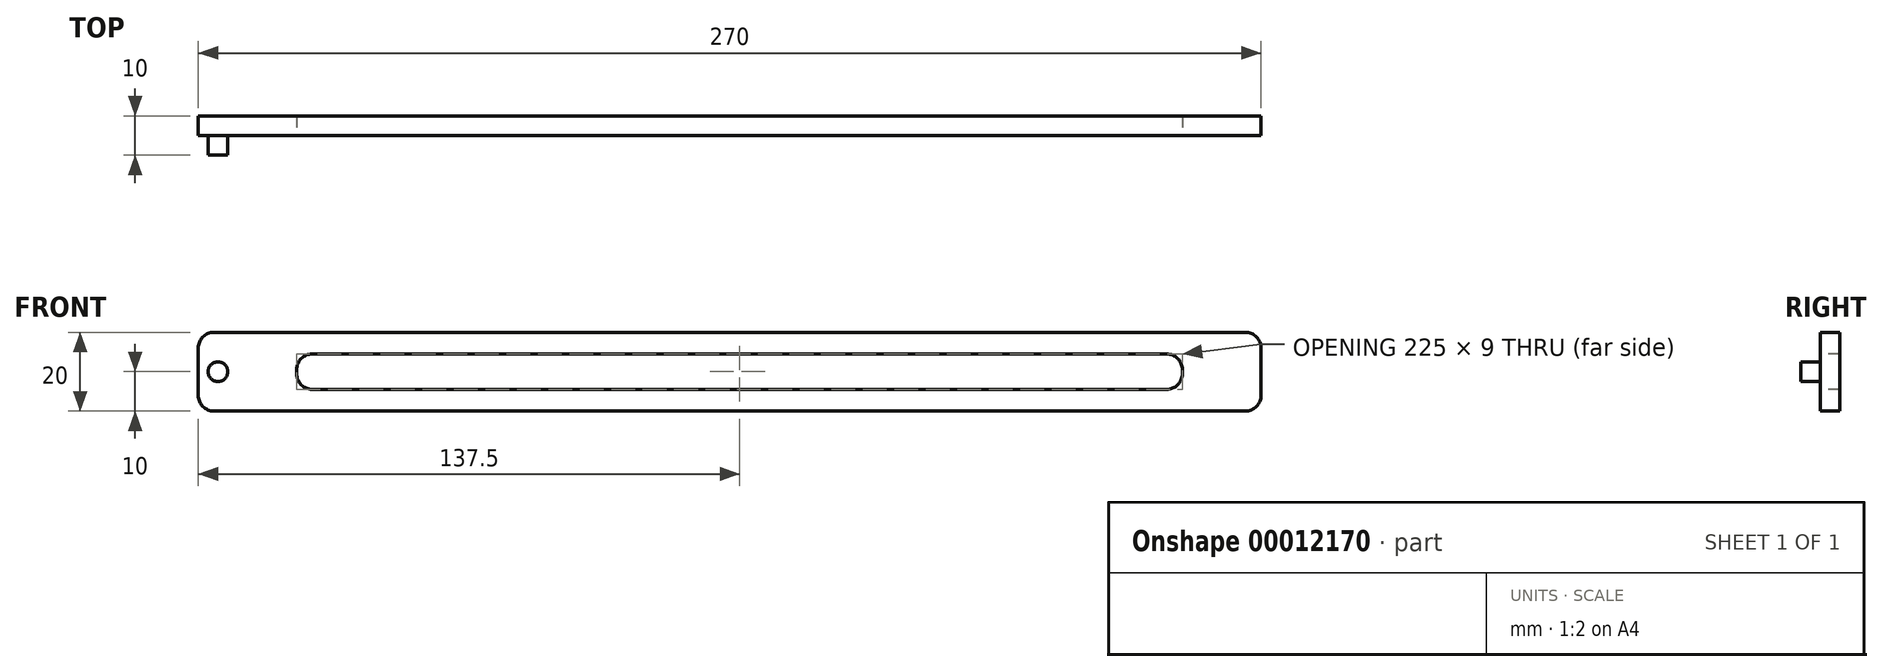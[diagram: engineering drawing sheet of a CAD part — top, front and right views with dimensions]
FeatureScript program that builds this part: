
annotation { "Feature Type Name" : "Feature", "Feature Type Description" : "" }
export const myFeature = defineFeature(function(context is Context, id is Id, definition is map)
    precondition{}
    {
        {
            var Q0;
            Q0=qCreatedBy(makeId("Right.planeOp"),FACE);
            var sketch = newSketch(context, id + "F0", { "sketchPlane" : qUnion([Q0])});
            skLineSegment(sketch, "E0.rect.bottom", {"start": v(2.5, -10) * mm, "end": v(-2.5, -10) * mm});
            skLineSegment(sketch, "E0.rect.top", {"start": v(2.5, 10) * mm, "end": v(-2.5, 10) * mm});
            skLineSegment(sketch, "E0.rect.left", {"start": v(2.5, -10) * mm, "end": v(2.5, 10) * mm});
            skLineSegment(sketch, "E0.rect.right", {"start": v(-2.5, -10) * mm, "end": v(-2.5, 10) * mm});
            skPoint(sketch, "E0.rect.middle", {"position": v(0, 0) * mm});
            skSolve(sketch);
        }
        {
            var Q0;
            Q0=makeQuery(id+"F0.imprint","IMPRINT",FACE,{"disambiguationData":[TD([[makeQuery(id+"F0.imprint","IMPRINT",EDGE,{"derivedFrom":sQuery(id+"F0.wireOp",EDGE,"E0.rect.bottom")}),-1.0]])]});
            extrude(context, id + "F1", {"entities" : qUnion([Q0]), "depth" : 110 * mm, "hasSecondDirection" : true, "secondDirectionOppositeDirection" : true, "secondDirectionDepth" : 160 * mm});
        }
        {
            var Q0;
            Q0=makeQuery(id+"F1.opExtrude","SWEPT_FACE",FACE,{"disambiguationData":[OSD([sQuery(id+"F0.wireOp",EDGE,"E0.rect.right")])]});
            var sketch = newSketch(context, id + "F2", { "sketchPlane" : qUnion([Q0])});
            skLineSegment(sketch, "E1", {"start": v(-160, 0) * mm, "end": v(-155, 0) * mm, "construction": true});
            skPoint(sketch, "E2.rect.middle", {"position": v(-155, 0) * mm});
            skCircle(sketch, "E3", {"center": v(-155, 0) * mm, "radius": 2.5 * mm});
            skSolve(sketch);
        }
        {
            var Q0;
            Q0=makeQuery(id+"F2.imprint","IMPRINT",FACE,{"disambiguationData":[TD([[makeQuery(id+"F2.imprint","IMPRINT",EDGE,{"derivedFrom":sQuery(id+"F2.wireOp",EDGE,"E3")}),1.0]])]});
            extrude(context, id + "F3", {"entities" : qUnion([Q0]), "operationType" : NewBodyOperationType.ADD, "depth" : 5 * mm});
        }
        {
            var Q0;
            Q0=makeQuery(id+"F1.opExtrude","SWEPT_FACE",FACE,{"disambiguationData":[OSD([sQuery(id+"F0.wireOp",EDGE,"E0.rect.right")])]});
            var sketch = newSketch(context, id + "F4", { "sketchPlane" : qUnion([Q0])});
            skLineSegment(sketch, "E4", {"start": v(110, 0) * mm, "end": v(90, 0) * mm, "construction": true});
            skLineSegment(sketch, "E5", {"start": v(90, 0) * mm, "end": v(90, 4.5) * mm, "construction": true});
            skLineSegment(sketch, "E6.bottom", {"start": v(90, 4.5) * mm, "end": v(-135, 4.5) * mm});
            skLineSegment(sketch, "E6.top", {"start": v(90, -4.5) * mm, "end": v(-135, -4.5) * mm});
            skLineSegment(sketch, "E6.left", {"start": v(90, 4.5) * mm, "end": v(90, -4.5) * mm});
            skLineSegment(sketch, "E6.right", {"start": v(-135, 4.5) * mm, "end": v(-135, -4.5) * mm});
            skSolve(sketch);
        }
        {
            var Q0;
            Q0=makeQuery(id+"F4.imprint","IMPRINT",FACE,{"disambiguationData":[TD([[makeQuery(id+"F4.imprint","IMPRINT",EDGE,{"derivedFrom":sQuery(id+"F4.wireOp",EDGE,"E6.bottom")}),1.0]])]});
            extrude(context, id + "F5", {"entities" : qUnion([Q0]), "operationType" : NewBodyOperationType.REMOVE, "endBound" : BoundingType.THROUGH_ALL, "oppositeDirection" : true, "depth" : 25 * mm});
        }
        {
            var Q0;
            Q0=makeQuery(id+"F1.opExtrude","CAP_EDGE",EDGE,{"disambiguationData":[OSD([sQuery(id+"F0.wireOp",EDGE,"E0.rect.top")])],"isStart":false});
            var Q1;
            Q1=makeQuery(id+"F1.opExtrude","CAP_EDGE",EDGE,{"disambiguationData":[OSD([sQuery(id+"F0.wireOp",EDGE,"E0.rect.bottom")])],"isStart":false});
            var Q2;
            Q2=makeQuery(id+"F1.opExtrude","CAP_EDGE",EDGE,{"disambiguationData":[OSD([sQuery(id+"F0.wireOp",EDGE,"E0.rect.top")])],"isStart":true});
            var Q3;
            Q3=makeQuery(id+"F1.opExtrude","CAP_EDGE",EDGE,{"disambiguationData":[OSD([sQuery(id+"F0.wireOp",EDGE,"E0.rect.bottom")])],"isStart":true});
            var Q4;
            Q4=makeQuery(id+"F5.boolean.opBoolean","COPY",EDGE,{"derivedFrom":makeQuery(id+"F5.opExtrude","SWEPT_EDGE",EDGE,{"disambiguationData":[OSD([sQuery(id+"F4.wireOp",EDGE,"E6.bottom"),sQuery(id+"F4.wireOp",EDGE,"E6.right")])]})});
            var Q5;
            Q5=makeQuery(id+"F5.boolean.opBoolean","COPY",EDGE,{"derivedFrom":makeQuery(id+"F5.opExtrude","SWEPT_EDGE",EDGE,{"disambiguationData":[OSD([sQuery(id+"F4.wireOp",EDGE,"E6.top"),sQuery(id+"F4.wireOp",EDGE,"E6.right")])]})});
            var Q6;
            Q6=makeQuery(id+"F5.boolean.opBoolean","COPY",EDGE,{"derivedFrom":makeQuery(id+"F5.opExtrude","SWEPT_EDGE",EDGE,{"disambiguationData":[OSD([sQuery(id+"F4.wireOp",EDGE,"E6.top"),sQuery(id+"F4.wireOp",EDGE,"E6.left")])]})});
            var Q7;
            Q7=makeQuery(id+"F5.boolean.opBoolean","COPY",EDGE,{"derivedFrom":makeQuery(id+"F5.opExtrude","SWEPT_EDGE",EDGE,{"disambiguationData":[OSD([sQuery(id+"F4.wireOp",EDGE,"E6.bottom"),sQuery(id+"F4.wireOp",EDGE,"E6.left")])]})});
            fillet(context, id + "F6", {"entities" : qUnion([Q0, Q1, Q2, Q3, Q4, Q5, Q6, Q7]), "radius" : 4 * mm, "tangentPropagation" : true, "allowEdgeOverflow" : false});
        }
    });
